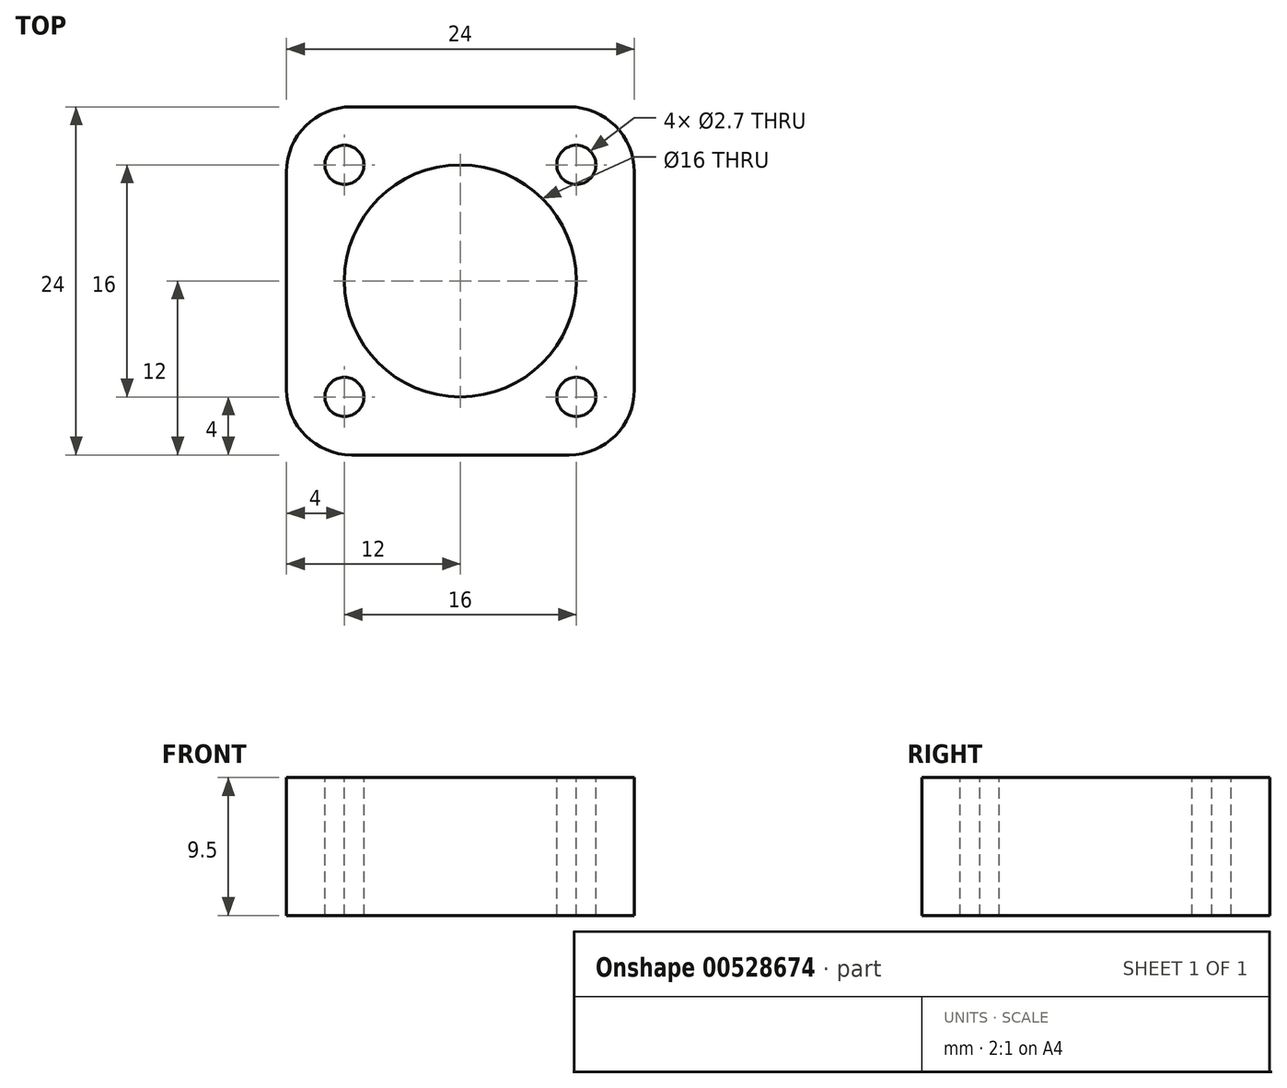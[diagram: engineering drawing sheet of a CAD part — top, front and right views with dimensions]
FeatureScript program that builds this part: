
annotation { "Feature Type Name" : "Feature", "Feature Type Description" : "" }
export const myFeature = defineFeature(function(context is Context, id is Id, definition is map)
    precondition{}
    {
        {
            var Q0;
            Q0=qCreatedBy(makeId("Top.planeOp"),FACE);
            var sketch = newSketch(context, id + "F0", { "sketchPlane" : qUnion([Q0])});
            skLineSegment(sketch, "E0.bottom", {"start": v(0, 0) * mm, "end": v(24, 0) * mm});
            skLineSegment(sketch, "E0.top", {"start": v(0, 24) * mm, "end": v(24, 24) * mm});
            skLineSegment(sketch, "E0.left", {"start": v(0, 0) * mm, "end": v(0, 24) * mm});
            skLineSegment(sketch, "E0.right", {"start": v(24, 0) * mm, "end": v(24, 24) * mm});
            skSolve(sketch);
        }
        {
            var Q0;
            Q0=makeQuery(id+"F0.imprint","IMPRINT",FACE,{"disambiguationData":[TD([[makeQuery(id+"F0.imprint","IMPRINT",EDGE,{"derivedFrom":sQuery(id+"F0.wireOp",EDGE,"E0.bottom")}),1.0]])]});
            extrude(context, id + "F1", {"entities" : qUnion([Q0]), "depth" : 9.5 * mm, "offsetDistance" : 25 * mm});
        }
        {
            var Q0;
            Q0=makeQuery(id+"F1.opExtrude","SWEPT_EDGE",EDGE,{"disambiguationData":[OSD([sQuery(id+"F0.wireOp",EDGE,"E0.bottom"),sQuery(id+"F0.wireOp",EDGE,"E0.left")])]});
            var Q1;
            Q1=makeQuery(id+"F1.opExtrude","SWEPT_EDGE",EDGE,{"disambiguationData":[OSD([sQuery(id+"F0.wireOp",EDGE,"E0.bottom"),sQuery(id+"F0.wireOp",EDGE,"E0.right")])]});
            var Q2;
            Q2=makeQuery(id+"F1.opExtrude","SWEPT_EDGE",EDGE,{"disambiguationData":[OSD([sQuery(id+"F0.wireOp",EDGE,"E0.top"),sQuery(id+"F0.wireOp",EDGE,"E0.right")])]});
            var Q3;
            Q3=makeQuery(id+"F1.opExtrude","SWEPT_EDGE",EDGE,{"disambiguationData":[OSD([sQuery(id+"F0.wireOp",EDGE,"E0.top"),sQuery(id+"F0.wireOp",EDGE,"E0.left")])]});
            fillet(context, id + "F2", {"entities" : qUnion([Q0, Q1, Q2, Q3]), "radius" : 4.5 * mm, "tangentPropagation" : true, "allowEdgeOverflow" : false});
        }
        {
            var Q0;
            Q0=makeQuery(id+"F1.opExtrude","CAP_FACE",FACE,{"disambiguationData":[OSD([sQuery(id+"F0.wireOp",EDGE,"E0.bottom"),sQuery(id+"F0.wireOp",EDGE,"E0.top"),sQuery(id+"F0.wireOp",EDGE,"E0.left"),sQuery(id+"F0.wireOp",EDGE,"E0.right")])],"isStart":false});
            var sketch = newSketch(context, id + "F3", { "sketchPlane" : qUnion([Q0])});
            skCircle(sketch, "E1", {"center": v(4, 4) * mm, "radius": 1.35 * mm});
            skCircle(sketch, "E2.0.1.0", {"center": v(4, 20) * mm, "radius": 1.35 * mm});
            skCircle(sketch, "E2.1.0.0", {"center": v(20, 4) * mm, "radius": 1.35 * mm});
            skCircle(sketch, "E2.1.1.0", {"center": v(20, 20) * mm, "radius": 1.35 * mm});
            skLineSegment(sketch, "E2.direction1", {"start": v(4, 4) * mm, "end": v(20, 4) * mm, "construction": true});
            skLineSegment(sketch, "E2.direction2", {"start": v(4, 4) * mm, "end": v(4, 20) * mm, "construction": true});
            skSolve(sketch);
        }
        {
            var Q0;
            Q0=makeQuery(id+"F3.imprint","IMPRINT",FACE,{"disambiguationData":[TD([[makeQuery(id+"F3.imprint","IMPRINT",EDGE,{"derivedFrom":sQuery(id+"F3.wireOp",EDGE,"E1")}),-1.0]])]});
            var sketch = newSketch(context, id + "F4", { "sketchPlane" : qUnion([Q0])});
            skCircle(sketch, "E3", {"center": v(12, 12) * mm, "radius": 8 * mm});
            skSolve(sketch);
        }
        {
            var Q0;
            Q0=qSketchRegion(id+"F4",true);
            extrude(context, id + "F5", {"entities" : qUnion([Q0]), "operationType" : NewBodyOperationType.REMOVE, "endBound" : BoundingType.THROUGH_ALL, "oppositeDirection" : true, "depth" : 12 * mm, "offsetDistance" : 25 * mm});
        }
        {
            var Q0;
            Q0=qSketchRegion(id+"F3",true);
            extrude(context, id + "F6", {"entities" : qUnion([Q0]), "operationType" : NewBodyOperationType.REMOVE, "endBound" : BoundingType.THROUGH_ALL, "oppositeDirection" : true, "depth" : 12 * mm, "offsetDistance" : 25 * mm});
        }
    });
